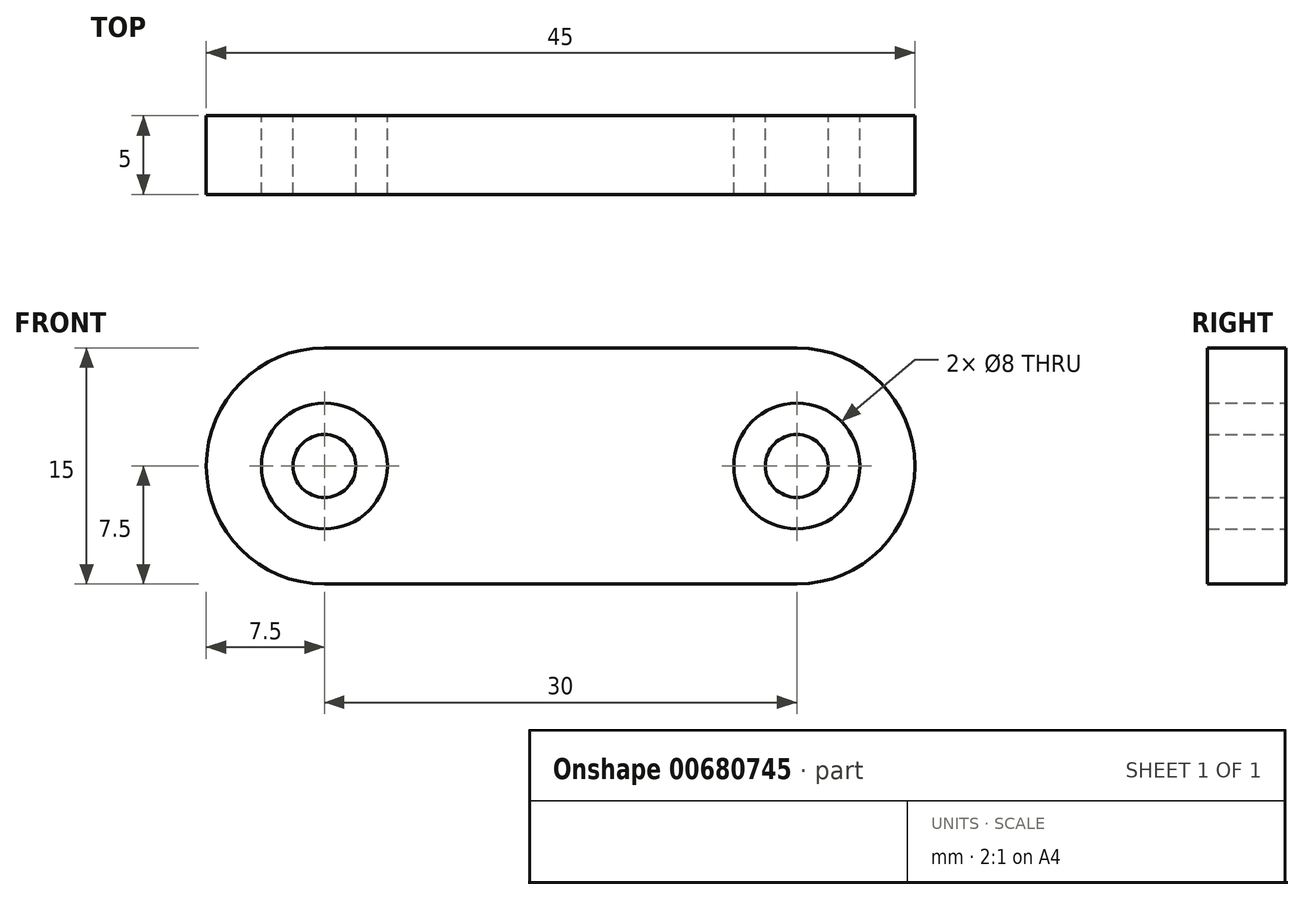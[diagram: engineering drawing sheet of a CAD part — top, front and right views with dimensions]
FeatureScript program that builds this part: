
annotation { "Feature Type Name" : "Feature", "Feature Type Description" : "" }
export const myFeature = defineFeature(function(context is Context, id is Id, definition is map)
    precondition{}
    {
        {
            var Q0;
            Q0=qCreatedBy(makeId("Front.planeOp"),FACE);
            var sketch = newSketch(context, id + "F0", { "sketchPlane" : qUnion([Q0])});
            skArc(sketch, "E0", {"start": v(0, 7.5) * mm, "mid": v(-7.5, 0) * mm, "end": v(0, -7.5) * mm});
            skCircle(sketch, "E1", {"center": v(0, 0) * mm, "radius": 4 * mm});
            skCircle(sketch, "E2", {"center": v(0, 0) * mm, "radius": 2 * mm});
            skLineSegment(sketch, "E3", {"start": v(0, -7.5) * mm, "end": v(30, -7.5) * mm});
            skCircle(sketch, "E4", {"center": v(30, 0) * mm, "radius": 2 * mm});
            skArc(sketch, "E5", {"start": v(30, -7.5) * mm, "mid": v(37.5, 0) * mm, "end": v(30, 7.5) * mm});
            skCircle(sketch, "E6", {"center": v(30, 0) * mm, "radius": 4 * mm});
            skLineSegment(sketch, "E7", {"start": v(0, 7.5) * mm, "end": v(30, 7.5) * mm});
            skSolve(sketch);
        }
        {
            var Q0;
            Q0=makeQuery(id+"F0.imprint","IMPRINT",FACE,{"disambiguationData":[TD([[makeQuery(id+"F0.imprint","IMPRINT",EDGE,{"derivedFrom":sQuery(id+"F0.wireOp",EDGE,"E2")}),1.0]])]});
            var Q1;
            Q1=makeQuery(id+"F0.imprint","IMPRINT",FACE,{"disambiguationData":[TD([[makeQuery(id+"F0.imprint","IMPRINT",EDGE,{"derivedFrom":sQuery(id+"F0.wireOp",EDGE,"E4")}),1.0]])]});
            var Q2;
            Q2=makeQuery(id+"F0.imprint","IMPRINT",FACE,{"disambiguationData":[TD([[makeQuery(id+"F0.imprint","IMPRINT",EDGE,{"derivedFrom":sQuery(id+"F0.wireOp",EDGE,"E0")}),1.0]])]});
            extrude(context, id + "F1", {"entities" : qUnion([Q0, Q1, Q2]), "depth" : 5 * mm, "offsetDistance" : 25.4 * mm});
        }
    });
